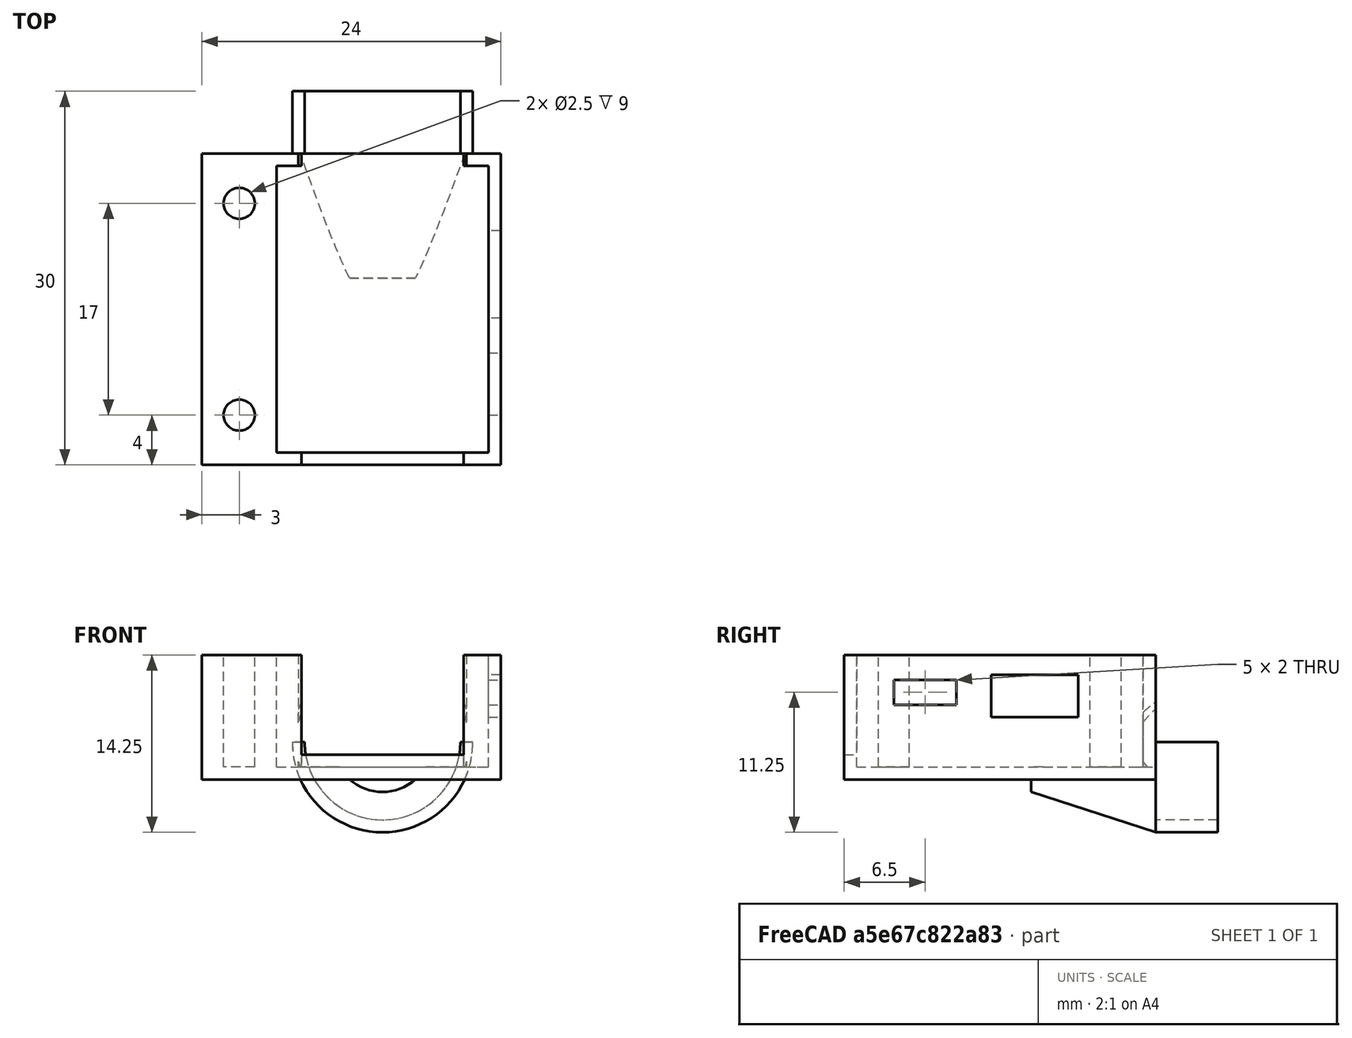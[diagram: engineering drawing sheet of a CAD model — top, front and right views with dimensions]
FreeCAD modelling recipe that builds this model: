
FCSTD DOCUMENT  (FreeCAD 0.18R16131 (Git))
Label: glowstick_case
License: All rights reserved
LicenseURL: http://en.wikipedia.org/wiki/All_rights_reserved
objects: Part::Box×11, Part::Cut×11, Part::Cylinder×4, Part::MultiFuse×4, Part::Cone×1
note: 31 computed .brp shape members not serialized (recipe doc carries the construction recipe); baked Part::Feature solids carry a one-line shape summary decoded from their .brp

FEATURE [Part::Box] Box  label="Cube"
  AttacherType = Attacher::AttachEngine3D
  Height = 12
  Length = 17
  Placement = pos=(1,0,1) rot=(0,0,1;0rad)
  Width = 23
FEATURE [Part::Box] Box001  label="Cube001"
  AttacherType = Attacher::AttachEngine3D
  Height = 10
  Length = 19
  Placement = pos=(0,-1,0) rot=(0,0,1;0rad)
  Width = 25
FEATURE [Part::Box] Box002  label="Cube002"
  AttacherType = Attacher::AttachEngine3D
  Height = 12
  Length = 13.5
  Placement = pos=(2.75,15,1) rot=(0,0,1;0rad)
  Width = 10
FEATURE [Part::Box] Box003  label="Cube003"
  AttacherType = Attacher::AttachEngine3D
  Height = 12
  Length = 13
  Placement = pos=(3,-1,2) rot=(0,0,1;0rad)
  Width = 13
FEATURE [Part::Cut] Cut
  Base = -> Box001
  Tool = -> Box
FEATURE [Part::Cut] Cut001
  Base = -> Cut
  Tool = -> Box003
FEATURE [Part::Cut] Cut002
  Base = -> Cut001
  Tool = -> Box002
FEATURE [Part::Box] Box004  label="Cube004"
  AttacherType = Attacher::AttachEngine3D
  Height = 10
  Length = 6.5
  Placement = pos=(15,10.8,5) rot=(0,0,1;0rad)
  Width = 7
FEATURE [Part::Cut] Cut003
  Base = -> Cut002
  Tool = -> Box004
FEATURE [Part::Cylinder] Cylinder
  Angle = 360
  AttacherType = Attacher::AttachEngine3D
  Height = 5
  Placement = pos=(9.5,29,3) rot=(1,0,0;1.5708rad)
  Radius = 6.25
FEATURE [Part::Cylinder] Cylinder001
  Angle = 360
  AttacherType = Attacher::AttachEngine3D
  Height = 5
  Placement = pos=(9.5,29,3) rot=(1,0,0;1.5708rad)
  Radius = 7.25
FEATURE [Part::Cut] Cut004
  Base = -> Cylinder001
  Tool = -> Cylinder
FEATURE [Part::Box] Box005  label="Cube005"
  AttacherType = Attacher::AttachEngine3D
  Height = 10
  Length = 20
  Placement = pos=(0,24,3) rot=(0,0,1;0rad)
  Width = 10
FEATURE [Part::Cut] Cut005
  Base = -> Cut004
  Tool = -> Box005
FEATURE [Part::MultiFuse] Fusion
  Shapes = -> [Cut003,Cut005]
FEATURE [Part::Cone] Cone
  Angle = 360
  AttacherType = Attacher::AttachEngine3D
  Height = 10
  Placement = pos=(9.5,14,3) rot=(1,0,0;-1.5708rad)
  Radius1 = 4
  Radius2 = 7.25
FEATURE [Part::Box] Box006  label="Cube006"
  AttacherType = Attacher::AttachEngine3D
  Height = 10
  Length = 15
  Placement = pos=(2,13,1) rot=(0,0,1;0rad)
  Width = 10
FEATURE [Part::Box] Box007  label="Cube007"
  AttacherType = Attacher::AttachEngine3D
  Height = 10
  Length = 13
  Placement = pos=(3,14,1) rot=(0,0,1;0rad)
  Width = 10
FEATURE [Part::Cut] Cut006
  Base = -> Cone
  Tool = -> Box006
FEATURE [Part::Cut] Cut007
  Base = -> Cut006
  Tool = -> Box007
FEATURE [Part::MultiFuse] Fusion001
  Shapes = -> [Cut007,Fusion]
FEATURE [Part::Box] Box008  label="Cube008"
  AttacherType = Attacher::AttachEngine3D
  Height = 10
  Length = 5
  Placement = pos=(-5,-1,0) rot=(0,0,1;0rad)
  Width = 25
FEATURE [Part::Box] Box009  label="Cube009"
  AttacherType = Attacher::AttachEngine3D
  Height = 2
  Length = 5
  Placement = pos=(15,3,6) rot=(0,0,1;0rad)
  Width = 5
FEATURE [Part::Cut] Cut008
  Base = -> Fusion001
  Tool = -> Box009
FEATURE [Part::Cylinder] Cylinder002
  Angle = 360
  AttacherType = Attacher::AttachEngine3D
  Height = 9
  Placement = pos=(-2,3,1) rot=(0,0,1;0rad)
  Radius = 1.25
FEATURE [Part::Cylinder] Cylinder003
  Angle = 360
  AttacherType = Attacher::AttachEngine3D
  Height = 9
  Placement = pos=(-2,20,1) rot=(0,0,1;0rad)
  Radius = 1.25
FEATURE [Part::MultiFuse] Fusion002
  Shapes = -> [Cut008,Box008]
FEATURE [Part::Cut] Cut009
  Base = -> Fusion002
  Tool = -> Cylinder002
FEATURE [Part::Cut] Cut010
  Base = -> Cut009
  Tool = -> Cylinder003
FEATURE [Part::Box] Box010  label="Cube010"
  AttacherType = Attacher::AttachEngine3D
  Height = 1.6
  Length = 1
  Placement = pos=(18,10,8.4) rot=(0,0,1;0rad)
  Width = 10
FEATURE [Part::MultiFuse] Fusion003
  Shapes = -> [Box010,Cut010]
